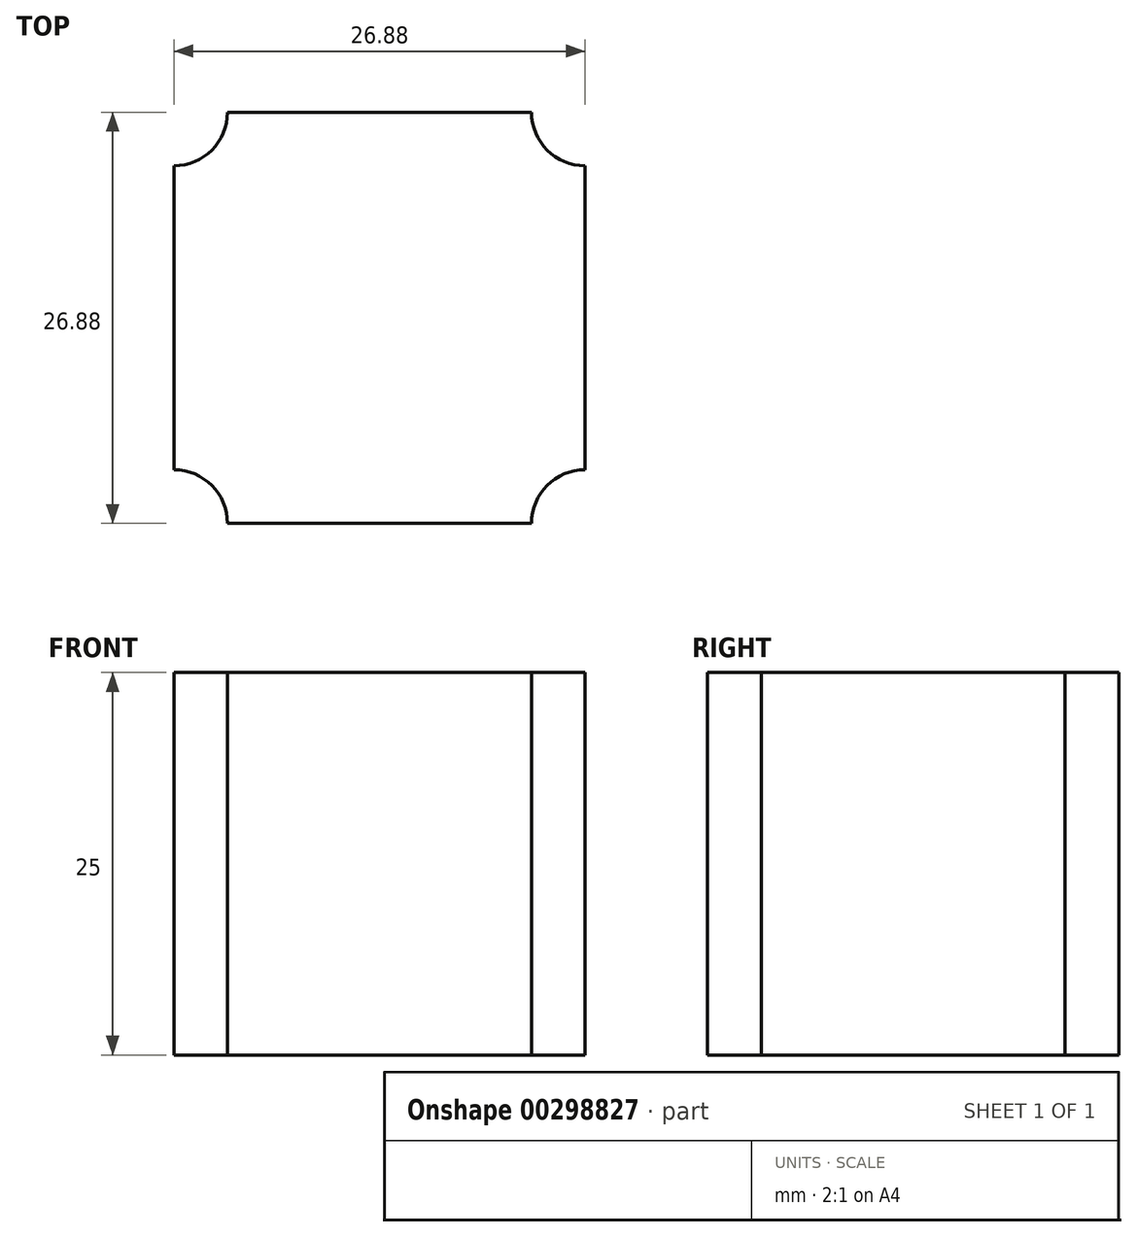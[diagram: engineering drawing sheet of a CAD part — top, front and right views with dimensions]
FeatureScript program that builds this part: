
annotation { "Feature Type Name" : "Feature", "Feature Type Description" : "" }
export const myFeature = defineFeature(function(context is Context, id is Id, definition is map)
    precondition{}
    {
        {
            var Q0;
            Q0=qCreatedBy(makeId("Top.planeOp"),FACE);
            var sketch = newSketch(context, id + "F0", { "sketchPlane" : qUnion([Q0])});
            skLineSegment(sketch, "E0.bottom", {"start": v(13.44, 13.44) * mm, "end": v(-13.44, 13.44) * mm});
            skLineSegment(sketch, "E0.top", {"start": v(13.44, -13.44) * mm, "end": v(-13.44, -13.44) * mm});
            skLineSegment(sketch, "E0.left", {"start": v(13.44, 13.44) * mm, "end": v(13.44, -13.44) * mm});
            skLineSegment(sketch, "E0.right", {"start": v(-13.44, 13.44) * mm, "end": v(-13.44, -13.44) * mm});
            skPoint(sketch, "E0.middle", {"position": v(0, 0) * mm});
            skCircle(sketch, "E1", {"center": v(-13.44, 13.44) * mm, "radius": 3.5 * mm});
            skCircle(sketch, "E2.MirrorC", {"center": v(13.44, 13.44) * mm, "radius": 3.5 * mm});
            skCircle(sketch, "E3.MirrorC", {"center": v(-13.44, -13.44) * mm, "radius": 3.5 * mm});
            skCircle(sketch, "E4.MirrorC", {"center": v(13.44, -13.44) * mm, "radius": 3.5 * mm});
            skPoint(sketch, "E5", {"position": v(-10.96, 15.9) * mm});
            skPoint(sketch, "E6", {"position": v(-15.9, 10.96) * mm});
            skLineSegment(sketch, "E7", {"start": v(-10.96, 15.9) * mm, "end": v(-15.9, 10.96) * mm});
            skLineSegment(sketch, "E8.MirrorCS", {"start": v(10.96, 15.9) * mm, "end": v(15.9, 10.96) * mm});
            skLineSegment(sketch, "E9.MirrorCS", {"start": v(-10.96, -15.9) * mm, "end": v(-15.9, -10.96) * mm});
            skLineSegment(sketch, "E10.MirrorCS", {"start": v(10.96, -15.9) * mm, "end": v(15.9, -10.96) * mm});
            skArc(sketch, "E11", {"start": v(-15.9, -10.96) * mm, "mid": v(-15.68, 0) * mm, "end": v(-15.9, 10.96) * mm});
            skSolve(sketch);
        }
        {
            var Q0;
            {var subQ5=sQuery(id+"F0.wireOp",EDGE,"E2.MirrorC");var subQ13=sQuery(id+"F0.wireOp",EDGE,"E0.bottom");var subQ15=makeQuery(id+"F0.imprint","INTERSECT",VERTEX,{"derivedFrom":[subQ13,subQ5]});Q0=makeQuery(id+"F0.imprint","IMPRINT",FACE,{"disambiguationData":[TD([[makeQuery(id+"F0.imprint","IMPRINT",EDGE,{"disambiguationData":[TD([[subQ15,-1.0]])],"derivedFrom":subQ13}),1.0]])]});}
            extrude(context, id + "F1", {"entities" : qUnion([Q0]), "depth" : 25 * mm});
        }
        {
            var Q0;
            Q0=makeQuery(id+"F1.opExtrude","SWEPT_BODY",BODY,{"disambiguationData":[OSD([sQuery(id+"F0.wireOp",EDGE,"E0.bottom"),sQuery(id+"F0.wireOp",EDGE,"E0.top"),sQuery(id+"F0.wireOp",EDGE,"E0.left"),sQuery(id+"F0.wireOp",EDGE,"E0.right"),sQuery(id+"F0.wireOp",EDGE,"E1"),sQuery(id+"F0.wireOp",EDGE,"E2.MirrorC"),sQuery(id+"F0.wireOp",EDGE,"E3.MirrorC"),sQuery(id+"F0.wireOp",EDGE,"E4.MirrorC")])]});
            var Q1;
            Q1=qCreatedBy(makeId("Origin.pointOp"),VERTEX);
            transform(context, id + "F2", {"entities" : qUnion([Q0]), "transformType" : TransformType.COPY});
        }
        {
            var Q0;
            Q0=makeQuery(id+"F1.opExtrude","SWEPT_BODY",BODY,{"disambiguationData":[OSD([sQuery(id+"F0.wireOp",EDGE,"E0.bottom"),sQuery(id+"F0.wireOp",EDGE,"E0.top"),sQuery(id+"F0.wireOp",EDGE,"E0.left"),sQuery(id+"F0.wireOp",EDGE,"E0.right"),sQuery(id+"F0.wireOp",EDGE,"E1"),sQuery(id+"F0.wireOp",EDGE,"E2.MirrorC"),sQuery(id+"F0.wireOp",EDGE,"E3.MirrorC"),sQuery(id+"F0.wireOp",EDGE,"E4.MirrorC")])]});
            transform(context, id + "F3", {"entities" : qUnion([Q0]), "transformType" : TransformType.COPY});
        }
    });
